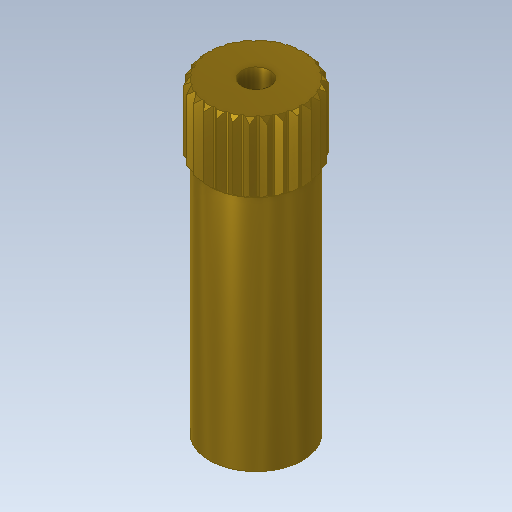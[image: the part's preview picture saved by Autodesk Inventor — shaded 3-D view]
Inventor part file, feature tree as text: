
AUTODESK INVENTOR PART (.ipt)
format: ipt  version: 2020 (Build 240168000, 168)  size: 367,104 bytes
history: native  units: mm
features: extrude x6, sketch x6, pattern_circular x2, plane x2, projected_geometry x2, other x1, mirror x1
ambient origin geometry x8: Origin, YZ Plane, XZ Plane, XY Plane, X Axis, Y Axis, Z Axis, Center Point
bodies: Body1 (feature_tree)
feature tree (20):
  other  "Sólido1"
  extrude  "Extrusión1"  Depth=13.5mm TaperAngle=0.0deg
  extrude  "Extrusión2"  Depth=4.0mm TaperAngle=0.0deg
  extrude  "Extrusión3"  Depth=4.0mm TaperAngle=360.0deg
  pattern_circular  "Patrón circular1"  Angle=45.0deg  [1 undecoded]
  plane  "Plano de trabajo1"
  extrude  "Extrusión4"  Depth=13.5mm
  pattern_circular  "Patrón circular2"  [2 undecoded]
  extrude  "Extrusión5"  Depth=13.5mm TaperAngle=360.0deg
  extrude  "Extrusión6"  Depth=13.5mm
  plane  "Plano de trabajo3"
  mirror  "Simetría2"
  sketch  "Boceto1"  dims[d0=5.8mm d1=13.5mm d2=0.0mm]
  sketch  "Boceto2"  dims[d3=0.3mm d4=4.0mm d5=0.0mm]
  projected_geometry  "Contorno proyectado1"
  sketch  "Boceto3"  dims[d9=4.0mm d10=0.0mm d11=260.0mm d12=360.0deg]
  projected_geometry  "Contorno proyectado2"
  sketch  "Boceto5"  dims[d21=0.3mm]
  sketch  "Boceto6"  dims[d22=13.962634mm]
  sketch  "Boceto7"  dims[d23=8.726646mm d25=45.0deg d26=0.25mm d27=0.7mm d28=0.0mm d29=260.0mm d30=360.0deg d32=1.6mm d33=4.0mm d34=0.0mm d36=13.5mm d37=0.0mm d38=5.3mm]
note: 3 required parameter values undecoded (feature->parameter linkage not recoverable at this tier; creation-order binding heuristic only, values carry confidence <= 0.55)
